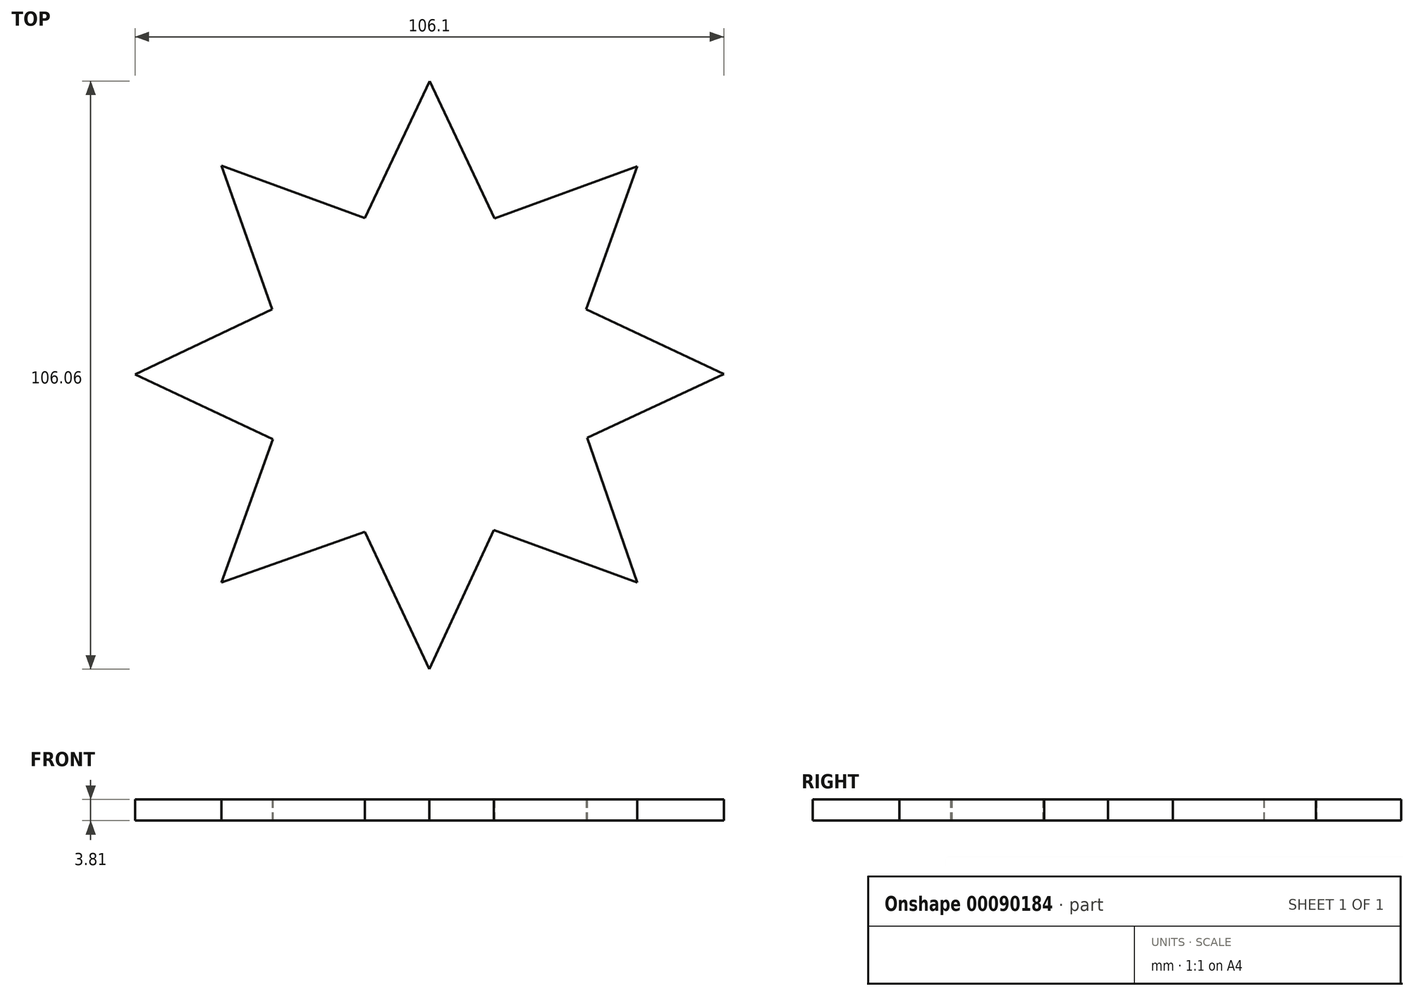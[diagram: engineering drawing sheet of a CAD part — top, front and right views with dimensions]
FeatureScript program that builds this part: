
annotation { "Feature Type Name" : "Feature", "Feature Type Description" : "" }
export const myFeature = defineFeature(function(context is Context, id is Id, definition is map)
    precondition{}
    {
        {
            var Q0;
            Q0=qCreatedBy(makeId("Top.planeOp"),FACE);
            var sketch = newSketch(context, id + "F0", { "sketchPlane" : qUnion([Q0])});
            skLineSegment(sketch, "E0", {"start": v(-38.74, 52.85) * mm, "end": v(-25.37, 24.62) * mm});
            skLineSegment(sketch, "E1", {"start": v(-25.37, 24.62) * mm, "end": v(4.05, 35.36) * mm});
            skLineSegment(sketch, "E2", {"start": v(4.05, 35.36) * mm, "end": v(-6.5, 5.88) * mm});
            skLineSegment(sketch, "E3", {"start": v(-6.5, 5.88) * mm, "end": v(21.86, -7.54) * mm});
            skLineSegment(sketch, "E4", {"start": v(21.86, -7.54) * mm, "end": v(-6.36, -20.69) * mm});
            skLineSegment(sketch, "E5", {"start": v(-6.36, -20.69) * mm, "end": v(3.93, -50.45) * mm});
            skLineSegment(sketch, "E6", {"start": v(3.93, -50.45) * mm, "end": v(-25.46, -39.68) * mm});
            skLineSegment(sketch, "E7", {"start": v(-25.46, -39.68) * mm, "end": v(-38.74, -68.32) * mm});
            skLineSegment(sketch, "E8", {"start": v(-38.74, -68.32) * mm, "end": v(-52.08, -39.9) * mm});
            skLineSegment(sketch, "E9", {"start": v(-52.08, -39.9) * mm, "end": v(-81.55, -50.34) * mm});
            skLineSegment(sketch, "E10", {"start": v(-81.55, -50.34) * mm, "end": v(-71, -20.92) * mm});
            skLineSegment(sketch, "E11", {"start": v(-71, -20.92) * mm, "end": v(-99.3, -7.54) * mm});
            skLineSegment(sketch, "E12", {"start": v(-99.3, -7.54) * mm, "end": v(-71.12, 5.84) * mm});
            skLineSegment(sketch, "E13", {"start": v(-71.12, 5.84) * mm, "end": v(-81.55, 35.44) * mm});
            skLineSegment(sketch, "E14", {"start": v(-81.55, 35.44) * mm, "end": v(-52.08, 24.65) * mm});
            skLineSegment(sketch, "E15", {"start": v(-52.08, 24.65) * mm, "end": v(-38.74, 52.85) * mm});
            skLineSegment(sketch, "E16.0", {"start": v(-50.43, 20.62) * mm, "end": v(-38.74, 45.34) * mm});
            skLineSegment(sketch, "E16.1", {"start": v(-76.26, 30.08) * mm, "end": v(-50.43, 20.62) * mm});
            skLineSegment(sketch, "E16.2", {"start": v(-67.13, 4.18) * mm, "end": v(-76.26, 30.08) * mm});
            skLineSegment(sketch, "E16.3", {"start": v(-91.8, -7.53) * mm, "end": v(-67.13, 4.18) * mm});
            skLineSegment(sketch, "E16.4", {"start": v(-67, -19.27) * mm, "end": v(-91.8, -7.53) * mm});
            skLineSegment(sketch, "E16.5", {"start": v(14.3, -7.52) * mm, "end": v(-10.35, -19) * mm});
            skLineSegment(sketch, "E16.6", {"start": v(-10.52, 4.22) * mm, "end": v(14.3, -7.52) * mm});
            skLineSegment(sketch, "E16.7", {"start": v(-1.29, 29.99) * mm, "end": v(-10.52, 4.22) * mm});
            skLineSegment(sketch, "E16.8", {"start": v(-27.02, 20.6) * mm, "end": v(-1.29, 29.99) * mm});
            skLineSegment(sketch, "E16.9", {"start": v(-10.35, -19) * mm, "end": v(-1.32, -45.1) * mm});
            skLineSegment(sketch, "E16.10", {"start": v(-1.32, -45.1) * mm, "end": v(-27.13, -35.65) * mm});
            skLineSegment(sketch, "E16.11", {"start": v(-27.13, -35.65) * mm, "end": v(-38.76, -60.72) * mm});
            skLineSegment(sketch, "E16.12", {"start": v(-38.76, -60.72) * mm, "end": v(-50.4, -35.9) * mm});
            skLineSegment(sketch, "E16.13", {"start": v(-50.4, -35.9) * mm, "end": v(-76.24, -45.05) * mm});
            skLineSegment(sketch, "E16.14", {"start": v(-38.74, 45.34) * mm, "end": v(-27.02, 20.6) * mm});
            skLineSegment(sketch, "E16.15", {"start": v(-76.24, -45.05) * mm, "end": v(-67, -19.27) * mm});
            skSolve(sketch);
        }
        {
            var Q0;
            Q0=makeQuery(id+"F0.imprint","IMPRINT",FACE,{"disambiguationData":[TD([[makeQuery(id+"F0.imprint","IMPRINT",EDGE,{"derivedFrom":sQuery(id+"F0.wireOp",EDGE,"E16.0")}),-1.0]])]});
            extrude(context, id + "F1", {"entities" : qUnion([Q0]), "depth" : 3.8 * mm});
        }
    });
